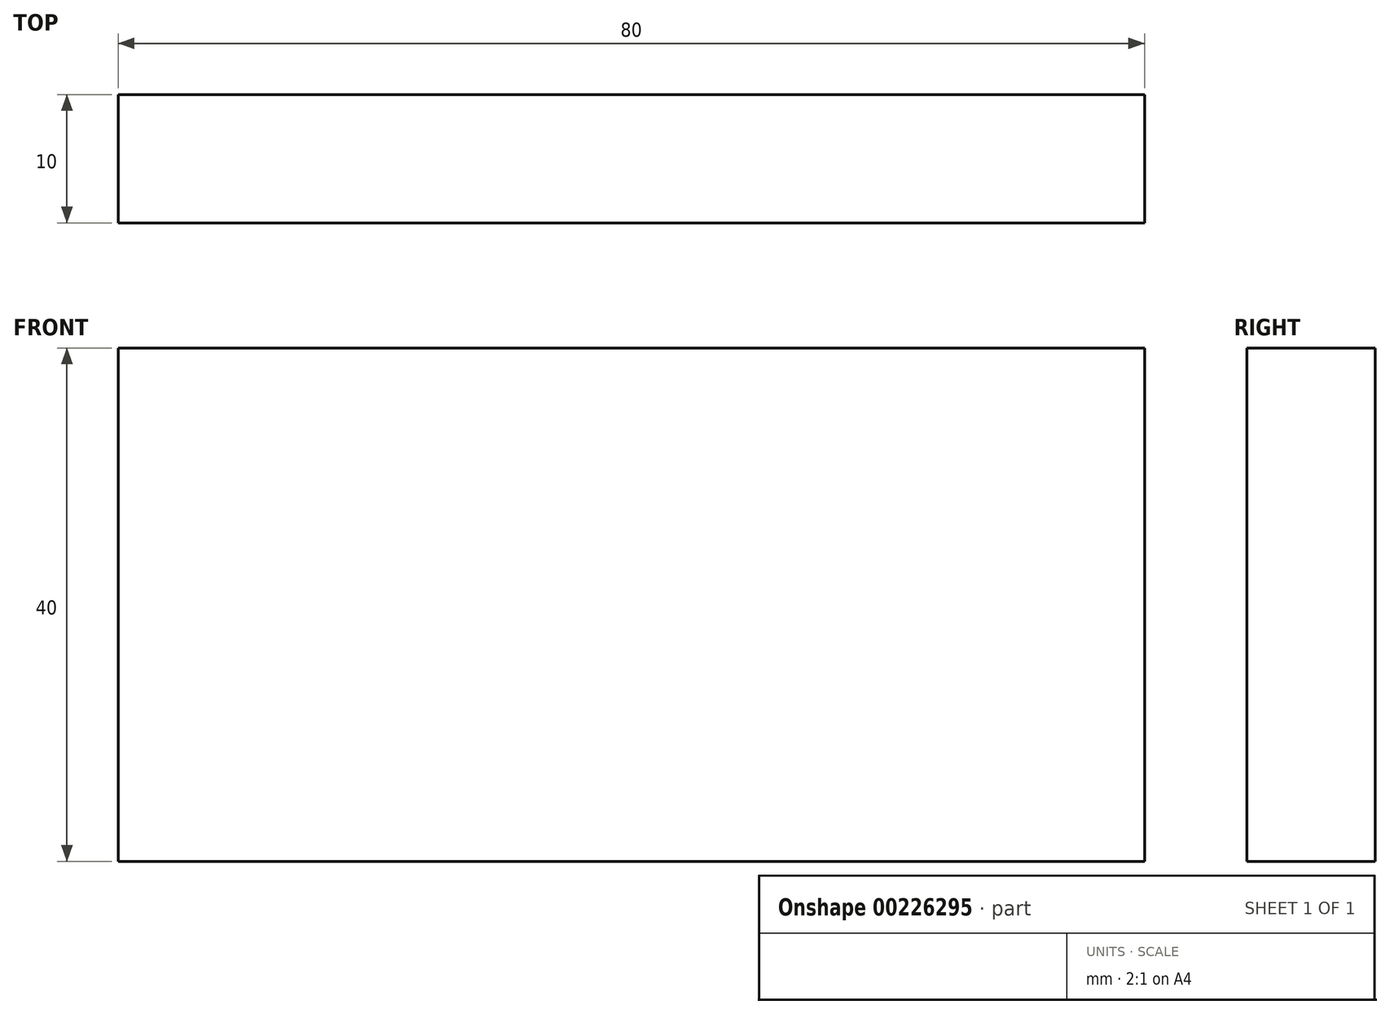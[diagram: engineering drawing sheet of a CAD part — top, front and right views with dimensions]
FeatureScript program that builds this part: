
annotation { "Feature Type Name" : "Feature", "Feature Type Description" : "" }
export const myFeature = defineFeature(function(context is Context, id is Id, definition is map)
    precondition{}
    {
        {
            var Q0;
            Q0=qCreatedBy(makeId("Front.planeOp"),FACE);
            var sketch = newSketch(context, id + "F0", { "sketchPlane" : qUnion([Q0])});
            skLineSegment(sketch, "E0.bottom", {"start": v(-40, 20) * mm, "end": v(40, 20) * mm});
            skLineSegment(sketch, "E0.top", {"start": v(-40, -20) * mm, "end": v(40, -20) * mm});
            skLineSegment(sketch, "E0.left", {"start": v(-40, 20) * mm, "end": v(-40, -20) * mm});
            skLineSegment(sketch, "E0.right", {"start": v(40, 20) * mm, "end": v(40, -20) * mm});
            skPoint(sketch, "E0.middle", {"position": v(0, 0) * mm});
            skSolve(sketch);
        }
        {
            var Q0;
            Q0=makeQuery(id+"F0.imprint","IMPRINT",FACE,{"disambiguationData":[TD([[makeQuery(id+"F0.imprint","IMPRINT",EDGE,{"derivedFrom":sQuery(id+"F0.wireOp",EDGE,"E0.bottom")}),-1.0]])]});
            extrude(context, id + "F1", {"entities" : qUnion([Q0]), "depth" : 10 * mm});
        }
        {
            var Q0;
            Q0=makeQuery(id+"F1.opExtrude","CAP_FACE",FACE,{"disambiguationData":[OSD([sQuery(id+"F0.wireOp",EDGE,"E0.bottom"),sQuery(id+"F0.wireOp",EDGE,"E0.top"),sQuery(id+"F0.wireOp",EDGE,"E0.left"),sQuery(id+"F0.wireOp",EDGE,"E0.right")])],"isStart":true});
            var sketch = newSketch(context, id + "F2", { "sketchPlane" : qUnion([Q0])});
            skCircle(sketch, "E1", {"center": v(-25.17, 10) * mm, "radius": 4 * mm});
            skCircle(sketch, "E2.MirrorC", {"center": v(25.17, 10) * mm, "radius": 4 * mm});
            skCircle(sketch, "E3.MirrorC", {"center": v(25.17, -10) * mm, "radius": 4 * mm});
            skCircle(sketch, "E4.MirrorC", {"center": v(-25.17, -10) * mm, "radius": 4 * mm});
            skSolve(sketch);
        }
        {
            var Q0;
            Q0=sQuery(id+"F2.wireOp",EDGE,"E3.MirrorC");
            var Q1;
            Q1=sQuery(id+"F2.wireOp",EDGE,"E2.MirrorC");
            var Q2;
            Q2=sQuery(id+"F2.wireOp",EDGE,"E1");
            var Q3;
            Q3=sQuery(id+"F2.wireOp",EDGE,"E4.MirrorC");
            extrude(context, id + "F3", {"bodyType" : ToolBodyType.SURFACE, "surfaceEntities" : qUnion([Q0, Q1, Q2, Q3]), "depth" : 25 * mm});
        }
    });
